# Revit family: EZ-LZ_8WSLSM
name_source: partatom
category: Plumbing Fixtures
units: mm (PartAtom-declared; Revit-internal decimal feet)

## family parameters
Always vertical = Yes
Cut with Voids When Loaded = No
OmniClass Number = 23.45.00.00
OmniClass Title = Sanitary, Laundry, and Cleaning Equipment
Part Type = Normal
Room Calculation Point = No
Round Connector Dimension = Use Diameter
Shared = No
Work Plane-Based = No

## types (1)
- EZ-LZ_8WSLSM
    Basin Material = Metal - Steel - Stainless - Chrome
    Description = EZ8WS & LZ8WS Series Bottle Filling Stations & Chillers
    Model = EZ-LZ_8WSLSM
    Panel Material = Metal - Steel - Stainless - Color 1
    Radius = 50 mm  [stored 0.164042 ft]
    Water Service Flow = 0.0 L/s
    Water Service Size Radius = 13 mm

note: [stored X ft] marks values corroborated as IEEE doubles in the binary element streams (Revit-internal decimal feet)

## geometry (parser evidence)
native form markers: Sweep x12
no freeform markers — native parametric forms only
